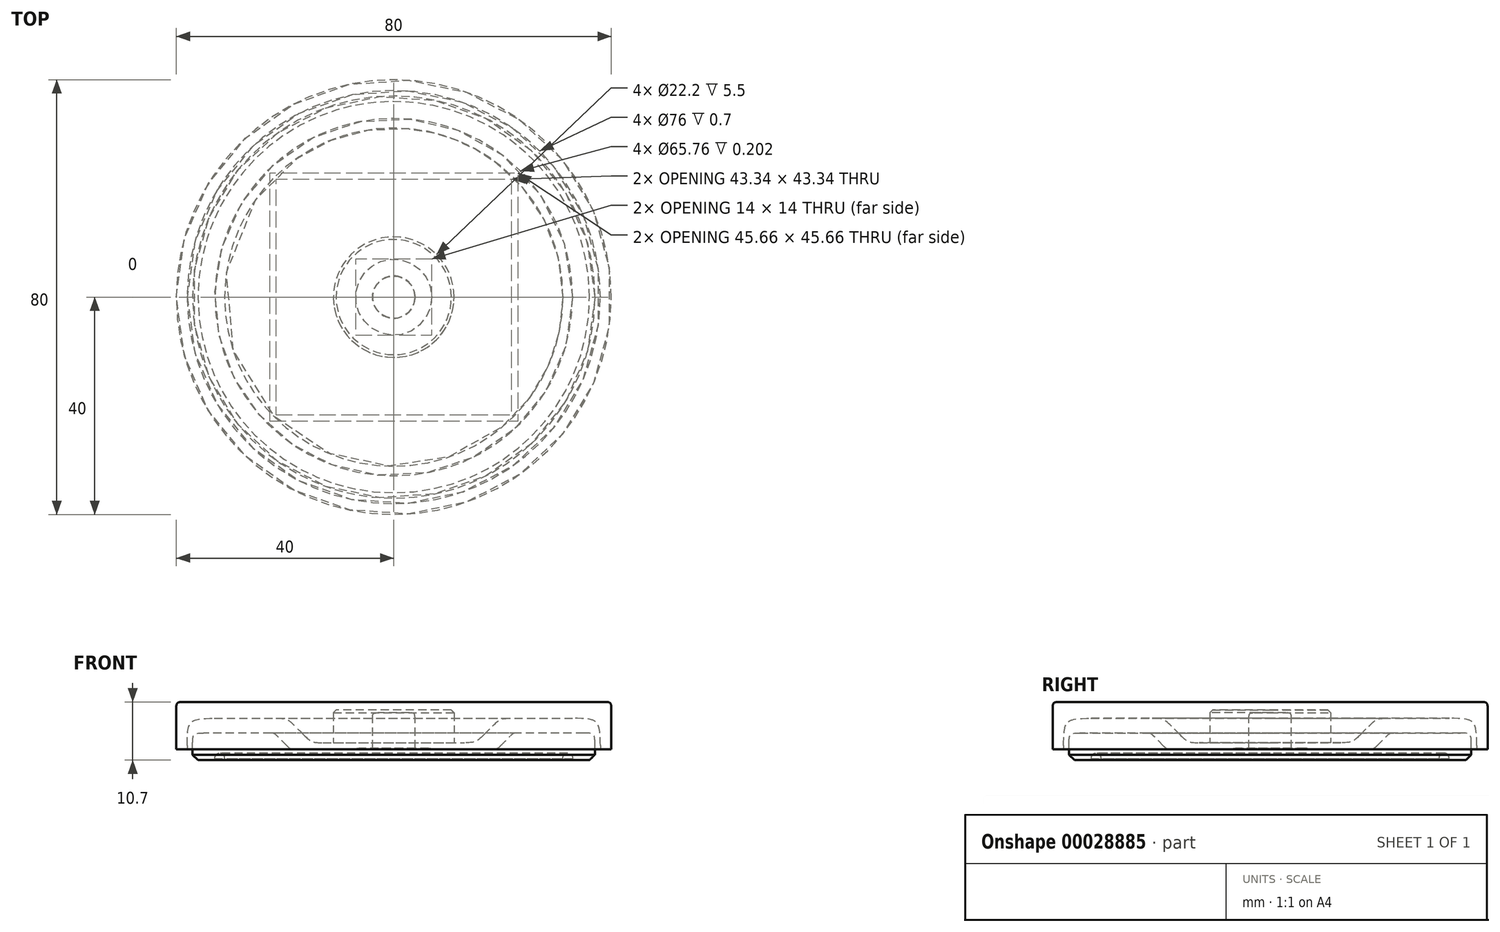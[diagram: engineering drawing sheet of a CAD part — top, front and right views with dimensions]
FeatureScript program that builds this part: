
annotation { "Feature Type Name" : "Feature", "Feature Type Description" : "" }
export const myFeature = defineFeature(function(context is Context, id is Id, definition is map)
    precondition{}
    {
        {
            var Q0;
            Q0=qCreatedBy(makeId("Top.planeOp"),FACE);
            var sketch = newSketch(context, id + "F0", { "sketchPlane" : qUnion([Q0])});
            skCircle(sketch, "E0", {"center": v(0, 0) * mm, "radius": 40 * mm, "construction": true});
            skSolve(sketch);
        }
        {
            var Q0;
            Q0=qCreatedBy(makeId("Right.planeOp"),FACE);
            var sketch = newSketch(context, id + "F1", { "sketchPlane" : qUnion([Q0])});
            skLineSegment(sketch, "E1", {"start": v(0, 0) * mm, "end": v(37, 0) * mm});
            skLineSegment(sketch, "E2", {"start": v(37, 0) * mm, "end": v(37, 5) * mm});
            skLineSegment(sketch, "E3", {"start": v(37, 5) * mm, "end": v(22, 5) * mm});
            skLineSegment(sketch, "E4", {"start": v(19, 2) * mm, "end": v(7, 2) * mm});
            skLineSegment(sketch, "E5", {"start": v(7, 2) * mm, "end": v(7, 2.2) * mm});
            skLineSegment(sketch, "E6", {"start": v(7, 2.2) * mm, "end": v(3.9, 2.2) * mm});
            skLineSegment(sketch, "E7", {"start": v(3.9, 2.2) * mm, "end": v(3.9, 8.7) * mm});
            skLineSegment(sketch, "E8", {"start": v(3.9, 8.7) * mm, "end": v(0, 8.7) * mm});
            skLineSegment(sketch, "E9", {"start": v(0, 8.7) * mm, "end": v(0, 0) * mm});
            skLineSegment(sketch, "E10", {"start": v(37, 0) * mm, "end": v(40, 0) * mm, "construction": true});
            skLineSegment(sketch, "E11", {"start": v(22, 5) * mm, "end": v(19, 2) * mm});
            skSolve(sketch);
        }
        {
            var Q0;
            Q0 = qSketchRegion(id + "F1", true);
            var Q1;
            Q1=sQuery(id+"F1.wireOp",EDGE,"E9");
            revolve(context, id + "F2", {"entities" : qUnion([Q0]), "axis" : qUnion([Q1]), "revolveType" : RevolveType.FULL});
        }
        {
            var Q0;
            Q0=qCreatedBy(makeId("Right.planeOp"),FACE);
            var sketch = newSketch(context, id + "F3", { "sketchPlane" : qUnion([Q0])});
            skLineSegment(sketch, "E12", {"start": v(0, 9.2) * mm, "end": v(0, 10.7) * mm});
            skLineSegment(sketch, "E13", {"start": v(0, 10.7) * mm, "end": v(40, 10.7) * mm});
            skLineSegment(sketch, "E14", {"start": v(40, 10.7) * mm, "end": v(40, 2) * mm});
            skLineSegment(sketch, "E15", {"start": v(40, 2) * mm, "end": v(38, 2) * mm});
            skLineSegment(sketch, "E16", {"start": v(38, 2) * mm, "end": v(38, 7.7) * mm});
            skLineSegment(sketch, "E17", {"start": v(38, 7.7) * mm, "end": v(19.6, 7.7) * mm});
            skLineSegment(sketch, "E18", {"start": v(19.6, 7.7) * mm, "end": v(15.1, 3.2) * mm});
            skLineSegment(sketch, "E19", {"start": v(15.1, 3.2) * mm, "end": v(11.1, 3.2) * mm});
            skLineSegment(sketch, "E20", {"start": v(11.1, 3.2) * mm, "end": v(11.1, 9.2) * mm});
            skLineSegment(sketch, "E21", {"start": v(11.1, 9.2) * mm, "end": v(0, 9.2) * mm});
            skLineSegment(sketch, "E22", {"start": v(40, 2) * mm, "end": v(40, 0) * mm, "construction": true});
            skSolve(sketch);
        }
        {
            var Q0;
            Q0 = qSketchRegion(id + "F3", true);
            var Q1;
            Q1=sQuery(id+"F3.wireOp",EDGE,"E12");
            revolve(context, id + "F4", {"entities" : qUnion([Q0]), "axis" : qUnion([Q1]), "revolveType" : RevolveType.FULL});
        }
        {
            var Q0;
            Q0=makeQuery(id+"F2.opRevolve","SWEPT_EDGE",EDGE,{"disambiguationData":[OSD([sQuery(id+"F1.wireOp",EDGE,"E5"),sQuery(id+"F1.wireOp",EDGE,"E6")])]});
            var Q1;
            Q1=makeQuery(id+"F2.opRevolve","SWEPT_EDGE",EDGE,{"disambiguationData":[OSD([sQuery(id+"F1.wireOp",EDGE,"E7"),sQuery(id+"F1.wireOp",EDGE,"E8")])]});
            fillet(context, id + "F5", {"entities" : qUnion([Q0, Q1]), "radius" : 1 * mm, "tangentPropagation" : true, "rho" : .7, "crossSection" : FilletCrossSection.CONIC, "allowEdgeOverflow" : false});
        }
        {
            var Q0;
            Q0=makeQuery(id+"F2.opRevolve","SWEPT_EDGE",EDGE,{"disambiguationData":[OSD([sQuery(id+"F1.wireOp",EDGE,"E3"),sQuery(id+"F1.wireOp",EDGE,"E11")])]});
            var Q1;
            Q1=makeQuery(id+"F2.opRevolve","SWEPT_EDGE",EDGE,{"disambiguationData":[OSD([sQuery(id+"F1.wireOp",EDGE,"E4"),sQuery(id+"F1.wireOp",EDGE,"E11")])]});
            var Q2;
            Q2=makeQuery(id+"F2.opRevolve","SWEPT_EDGE",EDGE,{"disambiguationData":[OSD([sQuery(id+"F1.wireOp",EDGE,"E2"),sQuery(id+"F1.wireOp",EDGE,"E3")])]});
            fillet(context, id + "F6", {"entities" : qUnion([Q0, Q1, Q2]), "radius" : 2 * mm, "tangentPropagation" : true, "rho" : .7, "crossSection" : FilletCrossSection.CONIC, "allowEdgeOverflow" : false});
        }
        {
            var Q0;
            Q0=makeQuery(id+"F4.opRevolve","SWEPT_EDGE",EDGE,{"disambiguationData":[OSD([sQuery(id+"F3.wireOp",EDGE,"E16"),sQuery(id+"F3.wireOp",EDGE,"E17")])]});
            var Q1;
            Q1=makeQuery(id+"F4.opRevolve","SWEPT_EDGE",EDGE,{"disambiguationData":[OSD([sQuery(id+"F3.wireOp",EDGE,"E17"),sQuery(id+"F3.wireOp",EDGE,"E18")])]});
            var Q2;
            Q2=makeQuery(id+"F4.opRevolve","SWEPT_EDGE",EDGE,{"disambiguationData":[OSD([sQuery(id+"F3.wireOp",EDGE,"E18"),sQuery(id+"F3.wireOp",EDGE,"E19")])]});
            fillet(context, id + "F7", {"entities" : qUnion([Q0, Q1, Q2]), "radius" : 5 * mm, "tangentPropagation" : true, "rho" : .7, "crossSection" : FilletCrossSection.CONIC, "allowEdgeOverflow" : false});
        }
        {
            var Q0;
            Q0=makeQuery(id+"F4.opRevolve","SWEPT_EDGE",EDGE,{"disambiguationData":[OSD([sQuery(id+"F3.wireOp",EDGE,"E20"),sQuery(id+"F3.wireOp",EDGE,"E21")])]});
            chamfer(context, id + "F8", {"entities" : qUnion([Q0]), "width" : .5 * mm, "tangentPropagation" : true});
        }
        {
            var Q0;
            Q0=makeQuery(id+"F4.opRevolve","SWEPT_EDGE",EDGE,{"disambiguationData":[OSD([sQuery(id+"F3.wireOp",EDGE,"E13"),sQuery(id+"F3.wireOp",EDGE,"E14")])]});
            fillet(context, id + "F9", {"entities" : qUnion([Q0]), "radius" : 1 * mm, "tangentPropagation" : true, "rho" : .6, "crossSection" : FilletCrossSection.CONIC, "allowEdgeOverflow" : false});
        }
        {
            var Q0;
            Q0=makeQuery(id+"F2.opRevolve","SWEPT_EDGE",EDGE,{"disambiguationData":[OSD([sQuery(id+"F1.wireOp",EDGE,"E1"),sQuery(id+"F1.wireOp",EDGE,"E2")])]});
            chamfer(context, id + "F10", {"entities" : qUnion([Q0]), "width" : 1 * mm, "tangentPropagation" : true});
        }
        {
            var Q0;
            Q0=makeQuery(id+"F2.opRevolve","SWEPT_FACE",FACE,{"disambiguationData":[OSD([sQuery(id+"F1.wireOp",EDGE,"E1")])]});
            var sketch = newSketch(context, id + "F11", { "sketchPlane" : qUnion([Q0])});
            skCircle(sketch, "E23", {"center": v(0, 0) * mm, "radius": 32 * mm});
            skSolve(sketch);
        }
        {
            var Q0;
            Q0=qCreatedBy(makeId("Right.planeOp"),FACE);
            var sketch = newSketch(context, id + "F12", { "sketchPlane" : qUnion([Q0])});
            skCircle(sketch, "E24", {"center": v(32, 0.4) * mm, "radius": 0.9 * mm});
            skLineSegment(sketch, "E25", {"start": v(32, 0.4) * mm, "end": v(32, 0) * mm, "construction": true});
            skLineSegment(sketch, "E26", {"start": v(32, 0) * mm, "end": v(32, -0.5) * mm, "construction": true});
            skSolve(sketch);
        }
        {
            var Q0;
            Q0 = qSketchRegion(id + "F12", true);
            var Q1;
            Q1=sQuery(id+"F11.wireOp",EDGE,"E23");
            sweep(context, id + "F13", {"operationType" : NewBodyOperationType.REMOVE, "profiles" : qUnion([Q0]), "path" : qUnion([Q1])});
        }
        {
            var Q0;
            Q0=makeQuery(id+"F13.boolean.opBoolean","INTERSECT",EDGE,{"disambiguationData":[OD(0.0)],"derivedFrom":[makeQuery(id+"F2.opRevolve","SWEPT_FACE",FACE,{"disambiguationData":[OSD([sQuery(id+"F1.wireOp",EDGE,"E1")])]}),makeQuery(id+"F13.opSweep","SWEPT_FACE",FACE,{"disambiguationData":[OSD([sQuery(id+"F11.wireOp",EDGE,"E23"),sQuery(id+"F12.wireOp",EDGE,"E24")])]})]});
            var Q1;
            Q1=makeQuery(id+"F13.boolean.opBoolean","INTERSECT",EDGE,{"disambiguationData":[OD(1.0)],"derivedFrom":[makeQuery(id+"F2.opRevolve","SWEPT_FACE",FACE,{"disambiguationData":[OSD([sQuery(id+"F1.wireOp",EDGE,"E1")])]}),makeQuery(id+"F13.opSweep","SWEPT_FACE",FACE,{"disambiguationData":[OSD([sQuery(id+"F11.wireOp",EDGE,"E23"),sQuery(id+"F12.wireOp",EDGE,"E24")])]})]});
            chamfer(context, id + "F14", {"entities" : qUnion([Q0, Q1]), "chamferType" : ChamferType.OFFSET_ANGLE, "width" : .1 * mm, "oppositeDirection" : false, "angle" : 90 * degree, "tangentPropagation" : true});
        }
    });
